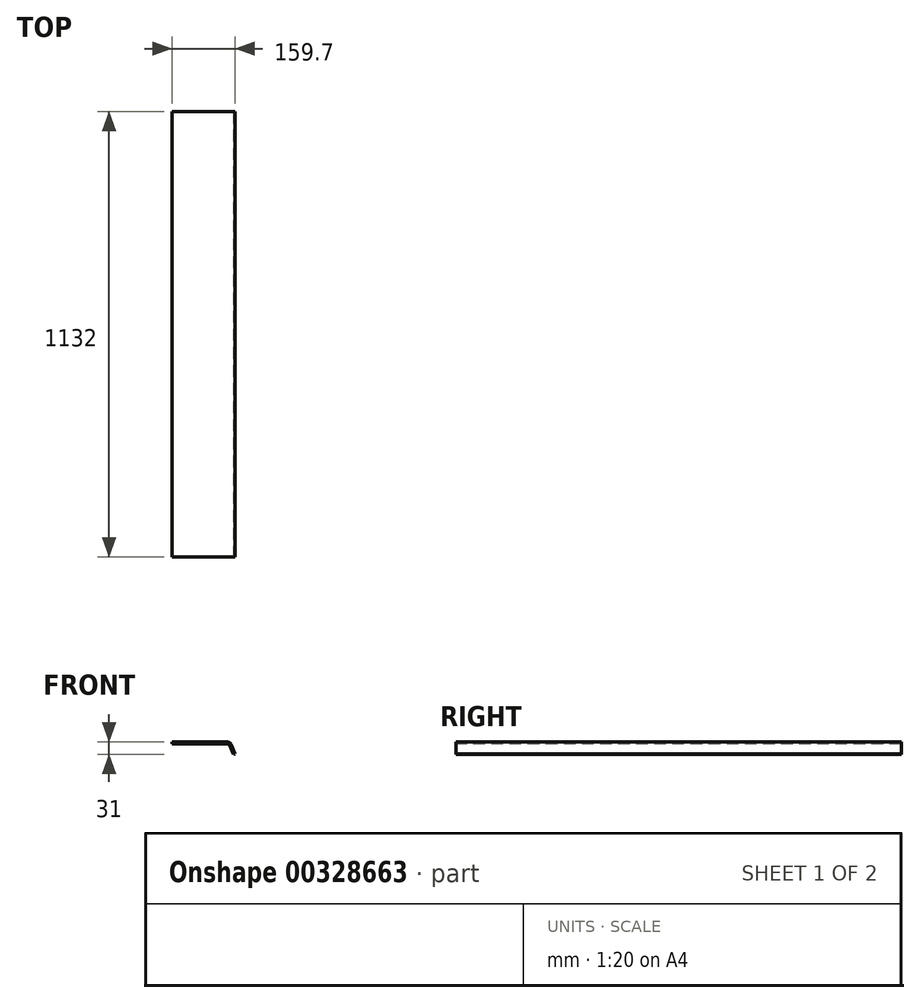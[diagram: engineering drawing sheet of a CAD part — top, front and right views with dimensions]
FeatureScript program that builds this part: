
annotation { "Feature Type Name" : "Feature", "Feature Type Description" : "" }
export const myFeature = defineFeature(function(context is Context, id is Id, definition is map)
    precondition{}
    {
        {
            var Q0;
            Q0=qCreatedBy(makeId("Front.planeOp"),FACE);
            var sketch = newSketch(context, id + "F0", { "sketchPlane" : qUnion([Q0])});
            skLineSegment(sketch, "E0.trimOffspring", {"start": v(0, 4) * mm, "end": v(141.48, 4) * mm});
            skLineSegment(sketch, "E1", {"start": v(0, 0) * mm, "end": v(141.48, 0) * mm});
            skLineSegment(sketch, "E2", {"start": v(146.1, -3.09) * mm, "end": v(156, -27) * mm});
            skPoint(sketch, "E3.visualSharp", {"position": v(144.82, 0) * mm});
            skArc(sketch, "E3.filletArc", {"start": v(146.1, -3.09) * mm, "mid": v(144.25, -0.84) * mm, "end": v(141.48, 0) * mm});
            skLineSegment(sketch, "E4", {"start": v(0, 0) * mm, "end": v(0, 4) * mm});
            skLineSegment(sketch, "E5", {"start": v(149.8, -1.56) * mm, "end": v(159.7, -25.47) * mm});
            skLineSegment(sketch, "E6", {"start": v(156, -27) * mm, "end": v(159.7, -25.47) * mm});
            skArc(sketch, "E7.filletArc", {"start": v(149.8, -1.56) * mm, "mid": v(146.48, 2.48) * mm, "end": v(141.48, 4) * mm});
            skSolve(sketch);
        }
        {
            var Q0;
            Q0=qSketchRegion(id+"F0",true);
            extrude(context, id + "F1", {"entities" : qUnion([Q0]), "oppositeDirection" : true, "depth" : 1132 * mm});
        }
    });
